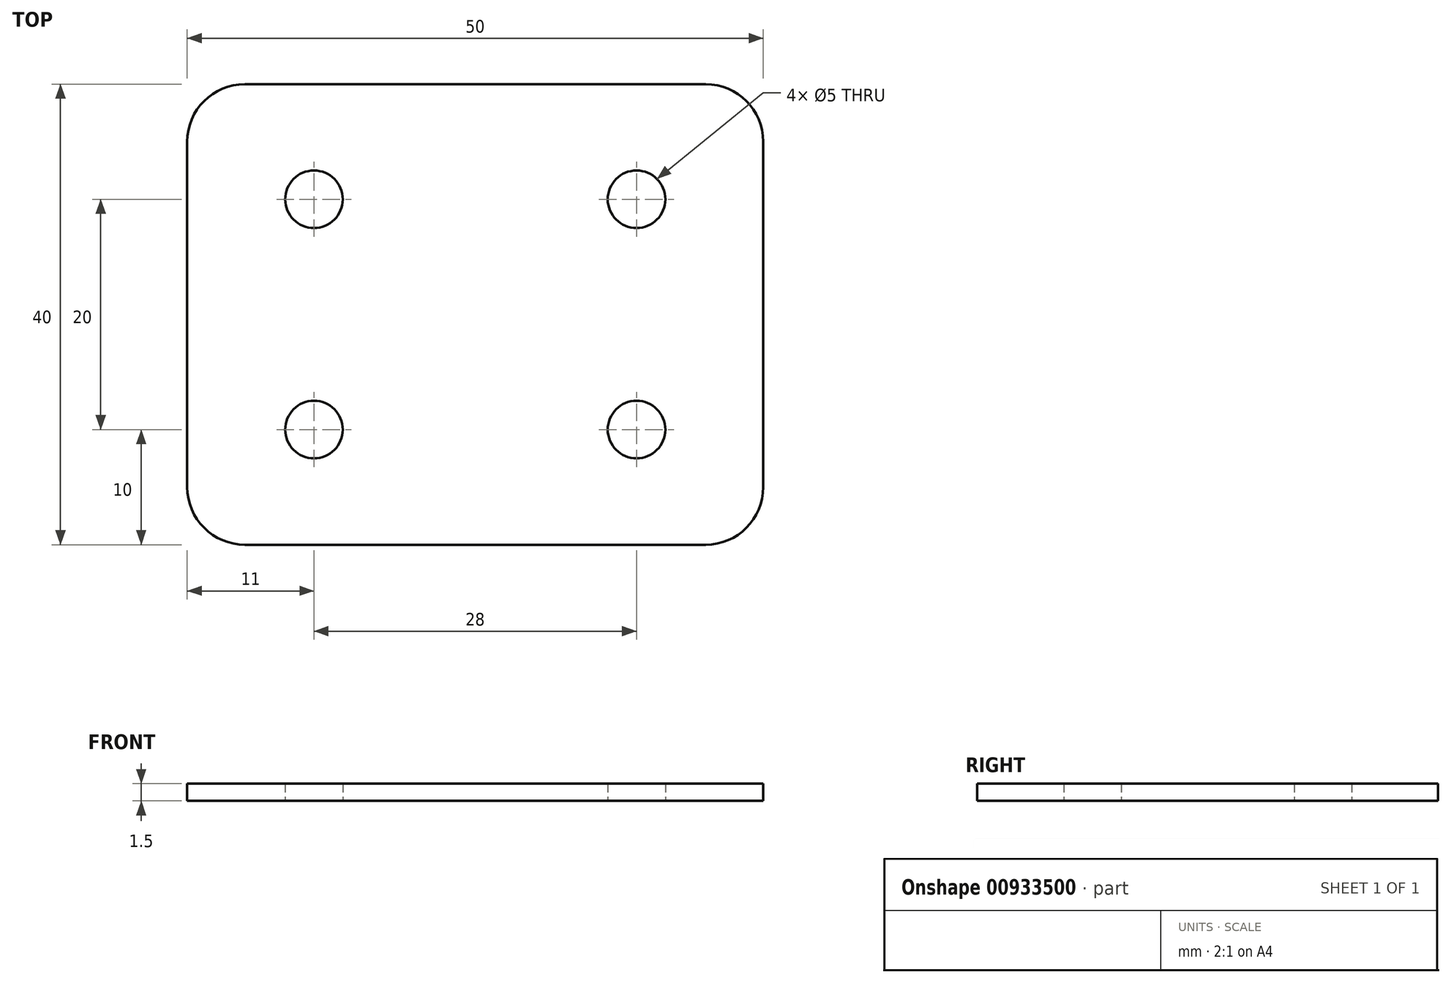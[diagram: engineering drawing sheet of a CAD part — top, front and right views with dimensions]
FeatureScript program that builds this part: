
annotation { "Feature Type Name" : "Feature", "Feature Type Description" : "" }
export const myFeature = defineFeature(function(context is Context, id is Id, definition is map)
    precondition{}
    {
        {
            var Q0;
            Q0=qCreatedBy(makeId("Top.planeOp"),FACE);
            var sketch = newSketch(context, id + "F0", { "sketchPlane" : qUnion([Q0])});
            skLineSegment(sketch, "E0", {"start": v(-20, 10) * mm, "end": v(20, 10) * mm});
            skLineSegment(sketch, "E1", {"start": v(-25, -25) * mm, "end": v(-25, 5) * mm});
            skLineSegment(sketch, "E2", {"start": v(-20, -30) * mm, "end": v(20, -30) * mm});
            skLineSegment(sketch, "E3", {"start": v(25, 5) * mm, "end": v(25, -25) * mm});
            skLineSegment(sketch, "E4", {"start": v(-26.2, -20) * mm, "end": v(31.2, -20) * mm, "construction": true});
            skCircle(sketch, "E5", {"center": v(-14, -20) * mm, "radius": 2.5 * mm});
            skCircle(sketch, "E6", {"center": v(14, -20) * mm, "radius": 2.5 * mm});
            skCircle(sketch, "E7", {"center": v(-14, 0) * mm, "radius": 2.5 * mm});
            skCircle(sketch, "E8", {"center": v(14, 0) * mm, "radius": 2.5 * mm});
            skPoint(sketch, "E9.visualSharp", {"position": v(-25, 10) * mm});
            skArc(sketch, "E9.filletArc", {"start": v(-20, 10) * mm, "mid": v(-23.54, 8.54) * mm, "end": v(-25, 5) * mm});
            skPoint(sketch, "E10.visualSharp", {"position": v(25, 10) * mm});
            skArc(sketch, "E10.filletArc", {"start": v(25, 5) * mm, "mid": v(23.54, 8.54) * mm, "end": v(20, 10) * mm});
            skPoint(sketch, "E11.visualSharp", {"position": v(25, -30) * mm});
            skArc(sketch, "E11.filletArc", {"start": v(20, -30) * mm, "mid": v(23.54, -28.54) * mm, "end": v(25, -25) * mm});
            skPoint(sketch, "E12.visualSharp", {"position": v(-25, -30) * mm});
            skArc(sketch, "E12.filletArc", {"start": v(-25, -25) * mm, "mid": v(-23.54, -28.54) * mm, "end": v(-20, -30) * mm});
            skSolve(sketch);
        }
        {
            var Q0;
            Q0 = qSketchRegion(id + "F0", true);
            extrude(context, id + "F1", {"entities" : qUnion([Q0]), "depth" : 1.5 * mm, "offsetDistance" : 25 * mm});
        }
    });
